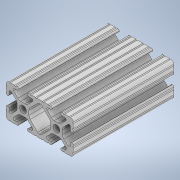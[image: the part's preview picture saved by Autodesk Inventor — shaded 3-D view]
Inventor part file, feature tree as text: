
AUTODESK INVENTOR PART (.ipt)
format: ipt  version: 2020 (Build 240168000, 168)  size: 334,336 bytes
history: native  units: in
note: dims shown in document units (in); Inventor stores cm internally (conversion verified against a paired STEP export)
features: sketch x2, extrude x1
ambient origin geometry x8: Origin, YZ Plane, XZ Plane, XY Plane, X Axis, Y Axis, Z Axis, Center Point
bodies: Solid1 (feature_tree)
feature tree (3):
  extrude  "Extrusion1"  [1 undecoded]
  sketch  "Sketch2"
  sketch  "Sketch1"  dims[d0=3.0in d1=0.0in]
note: 1 required parameter value undecoded (feature->parameter linkage not recoverable at this tier; creation-order binding heuristic only, values carry confidence <= 0.55)
